# Revit family: RATIO SQUARE 29H DG-TD606029
name_source: partatom
category: 家具
revit_build: Autodesk Revit 2016 (Build: 20150220_1215(x64)
units: mm (PartAtom-declared; Revit-internal decimal feet)

## family parameters
OmniClass 标题 = Residential Tables and Cabinets
OmniClass 编号 = 23.40.20.14.17
共享 = 是
加载时剪切的空心 = 否
基于工作平面 = 否
总是垂直 = 是
房间计算点 = 否

## types (3) — shared parameters
Base Material = Wood - Birch
Top Material = Laminate - Ivory, Matte

## per-type parameters (varying)
| type | Height | Length | Width |
| 0610 x 0160mm | 762  [stored 2.5 ft] | 610  [stored 2.00131 ft] | 610  [stored 2.00131 ft] |
| 0762 x 0762mm | 457  [stored 1.49934 ft] | 762  [stored 2.5 ft] | 762  [stored 2.5 ft] |
| 0610 x 0915mm | 762  [stored 2.5 ft] | 610  [stored 2.00131 ft] | 915 |

note: [stored X ft] marks values corroborated as IEEE doubles in the binary element streams (Revit-internal decimal feet)

## geometry (parser evidence)
native form markers: Sweep x1
no freeform markers — native parametric forms only
